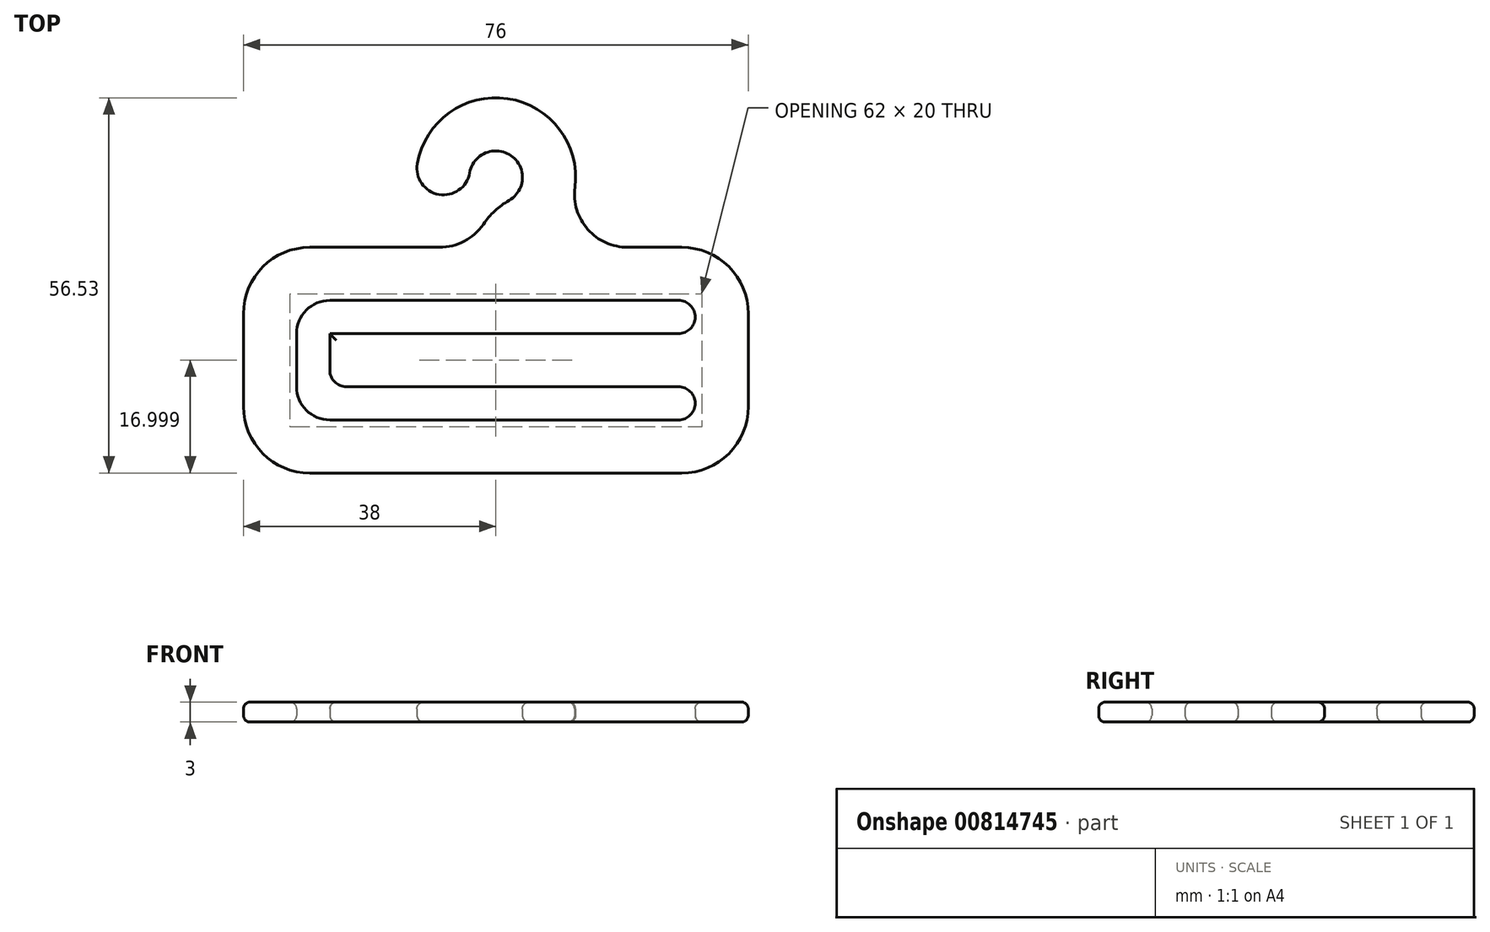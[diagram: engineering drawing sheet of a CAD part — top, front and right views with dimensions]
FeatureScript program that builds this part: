
annotation { "Feature Type Name" : "Feature", "Feature Type Description" : "" }
export const myFeature = defineFeature(function(context is Context, id is Id, definition is map)
    precondition{}
    {
        {
            var Q0;
            Q0=qCreatedBy(makeId("Top.planeOp"),FACE);
            var sketch = newSketch(context, id + "F0", { "sketchPlane" : qUnion([Q0])});
            skPoint(sketch, "E0.visualSharp", {"position": v(0, -8) * mm});
            skArc(sketch, "E0.filletArc", {"start": v(4, -6.93) * mm, "mid": v(2.08, -8.47) * mm, "end": v(0.72, -10.53) * mm, "construction": true});
            skArc(sketch, "E1", {"start": v(4, -6.93) * mm, "mid": v(4.58, 6.56) * mm, "end": v(-7.88, 1.37) * mm, "construction": true});
            skPoint(sketch, "E2", {"position": v(-7.88, 1.37) * mm});
            skArc(sketch, "E3.1.right", {"start": v(2, -3.46) * mm, "mid": v(-0.15, -5.05) * mm, "end": v(-1.9, -7.06) * mm});
            skArc(sketch, "E3.2.endCap", {"start": v(-3.94, 0.68) * mm, "mid": v(-8.57, -2.57) * mm, "end": v(-11.82, 2.05) * mm});
            skArc(sketch, "E3.2.left", {"start": v(2, -3.46) * mm, "mid": v(2.29, 3.28) * mm, "end": v(-3.94, 0.68) * mm});
            skArc(sketch, "E3.2.right", {"start": v(11.9, -1.52) * mm, "mid": v(1.78, 11.87) * mm, "end": v(-11.82, 2.05) * mm});
            skLineSegment(sketch, "E4.bottom", {"start": v(28, -10.53) * mm, "end": v(19.84, -10.53) * mm});
            skLineSegment(sketch, "E4.top", {"start": v(28, -44.53) * mm, "end": v(-28, -44.53) * mm});
            skLineSegment(sketch, "E4.left", {"start": v(38, -20.53) * mm, "end": v(38, -34.53) * mm});
            skLineSegment(sketch, "E4.right", {"start": v(-38, -20.53) * mm, "end": v(-38, -34.53) * mm});
            skPoint(sketch, "E4.middle", {"position": v(0, -27.53) * mm});
            skLineSegment(sketch, "E5", {"start": v(-30, -23.53) * mm, "end": v(-30, -31.53) * mm});
            skLineSegment(sketch, "E6", {"start": v(-25, -36.53) * mm, "end": v(27.5, -36.53) * mm});
            skLineSegment(sketch, "E7", {"start": v(30, -34.03) * mm, "end": v(30, -34.03) * mm});
            skLineSegment(sketch, "E8", {"start": v(27.5, -31.53) * mm, "end": v(-22.5, -31.53) * mm});
            skLineSegment(sketch, "E9", {"start": v(-25, -29.03) * mm, "end": v(-25, -23.53) * mm});
            skLineSegment(sketch, "E10", {"start": v(-25.03, -23.53) * mm, "end": v(27.5, -23.53) * mm});
            skLineSegment(sketch, "E11", {"start": v(30, -21.03) * mm, "end": v(30, -21.03) * mm});
            skLineSegment(sketch, "E12", {"start": v(27.5, -18.53) * mm, "end": v(-25, -18.53) * mm});
            skPoint(sketch, "E13.visualSharp", {"position": v(-38, -10.53) * mm});
            skArc(sketch, "E13.filletArc", {"start": v(-28, -10.53) * mm, "mid": v(-35.07, -13.46) * mm, "end": v(-38, -20.53) * mm});
            skPoint(sketch, "E14.visualSharp", {"position": v(-30, -18.53) * mm});
            skArc(sketch, "E14.filletArc", {"start": v(-25, -18.53) * mm, "mid": v(-28.54, -20) * mm, "end": v(-30, -23.53) * mm});
            skPoint(sketch, "E15.visualSharp", {"position": v(-38, -44.53) * mm});
            skArc(sketch, "E15.filletArc", {"start": v(-38, -34.53) * mm, "mid": v(-35.07, -41.6) * mm, "end": v(-28, -44.53) * mm});
            skPoint(sketch, "E16.visualSharp", {"position": v(-30, -36.53) * mm});
            skArc(sketch, "E16.filletArc", {"start": v(-30, -31.53) * mm, "mid": v(-28.54, -35.07) * mm, "end": v(-25, -36.53) * mm});
            skArc(sketch, "E17.filletArc", {"start": v(-25, -29.03) * mm, "mid": v(-24.27, -30.8) * mm, "end": v(-22.5, -31.53) * mm});
            skPoint(sketch, "E18.visualSharp", {"position": v(38, -44.53) * mm});
            skArc(sketch, "E18.filletArc", {"start": v(28, -44.53) * mm, "mid": v(35.07, -41.6) * mm, "end": v(38, -34.53) * mm});
            skLineSegment(sketch, "E19", {"start": v(30, -23.53) * mm, "end": v(30, -31.53) * mm, "construction": true});
            skPoint(sketch, "E20.visualSharp", {"position": v(30, -31.53) * mm});
            skArc(sketch, "E20.filletArc", {"start": v(30, -34.03) * mm, "mid": v(29.27, -32.26) * mm, "end": v(27.5, -31.53) * mm});
            skPoint(sketch, "E21.visualSharp", {"position": v(30, -36.53) * mm});
            skArc(sketch, "E21.filletArc", {"start": v(27.5, -36.53) * mm, "mid": v(29.27, -35.8) * mm, "end": v(30, -34.03) * mm});
            skPoint(sketch, "E22.visualSharp", {"position": v(30, -18.53) * mm});
            skArc(sketch, "E22.filletArc", {"start": v(30, -21.03) * mm, "mid": v(29.27, -19.26) * mm, "end": v(27.5, -18.53) * mm});
            skPoint(sketch, "E23.visualSharp", {"position": v(30, -23.53) * mm});
            skArc(sketch, "E23.filletArc", {"start": v(27.5, -23.53) * mm, "mid": v(29.27, -22.8) * mm, "end": v(30, -21.03) * mm});
            skPoint(sketch, "E24.visualSharp", {"position": v(38, -10.53) * mm});
            skArc(sketch, "E24.filletArc", {"start": v(38, -20.53) * mm, "mid": v(35.07, -13.46) * mm, "end": v(28, -10.53) * mm});
            skArc(sketch, "E25", {"start": v(0.72, -10.53) * mm, "mid": v(0.18, -12.15) * mm, "end": v(0, -13.86) * mm, "construction": true});
            skLineSegment(sketch, "E26.trimOffspring", {"start": v(-8.48, -10.53) * mm, "end": v(-28, -10.53) * mm});
            skPoint(sketch, "E27.visualSharp", {"position": v(-3.53, -10.53) * mm});
            skArc(sketch, "E27.filletArc", {"start": v(-8.48, -10.53) * mm, "mid": v(-4.76, -9.61) * mm, "end": v(-1.9, -7.06) * mm});
            skPoint(sketch, "E28.visualSharp", {"position": v(5.75, -10.53) * mm});
            skArc(sketch, "E28.filletArc", {"start": v(11.9, -1.52) * mm, "mid": v(13.84, -7.82) * mm, "end": v(19.84, -10.53) * mm});
            skLineSegment(sketch, "E29", {"start": v(-25, -23.53) * mm, "end": v(-22.66, -20.72) * mm});
            skSolve(sketch);
        }
        {
            var Q0;
            Q0=qSketchRegion(id+"F0",true);
            extrude(context, id + "F1", {"entities" : qUnion([Q0]), "depth" : 3 * mm, "offsetDistance" : 25 * mm});
        }
        {
            var Q0;
            Q0=makeQuery(id+"F0.imprint","IMPRINT",FACE,{"disambiguationData":[TD([[makeQuery(id+"F0.imprint","IMPRINT",EDGE,{"derivedFrom":sQuery(id+"F0.wireOp",EDGE,"E5")}),1.0]])]});
            extrude(context, id + "F2", {"entities" : qUnion([Q0]), "operationType" : NewBodyOperationType.REMOVE, "oppositeDirection" : true, "depth" : 3 * mm, "offsetDistance" : 25 * mm});
        }
        {
            var Q0;
            Q0=makeQuery(id+"F1.opExtrude","CAP_EDGE",EDGE,{"disambiguationData":[OSD([sQuery(id+"F0.wireOp",EDGE,"E8")])],"isStart":false});
            var Q1;
            Q1=makeQuery(id+"F1.opExtrude","CAP_EDGE",EDGE,{"disambiguationData":[OSD([sQuery(id+"F0.wireOp",EDGE,"E28.filletArc")])],"isStart":false});
            var Q2;
            Q2=makeQuery(id+"F1.opExtrude","CAP_EDGE",EDGE,{"disambiguationData":[OSD([sQuery(id+"F0.wireOp",EDGE,"E12")])],"isStart":true});
            var Q3;
            Q3=makeQuery(id+"F1.opExtrude","CAP_EDGE",EDGE,{"disambiguationData":[OSD([sQuery(id+"F0.wireOp",EDGE,"E3.2.endCap")])],"isStart":true});
            fillet(context, id + "F3", {"entities" : qUnion([Q0, Q1, Q2, Q3]), "radius" : 1 * mm, "tangentPropagation" : true, "allowEdgeOverflow" : false});
        }
    });
